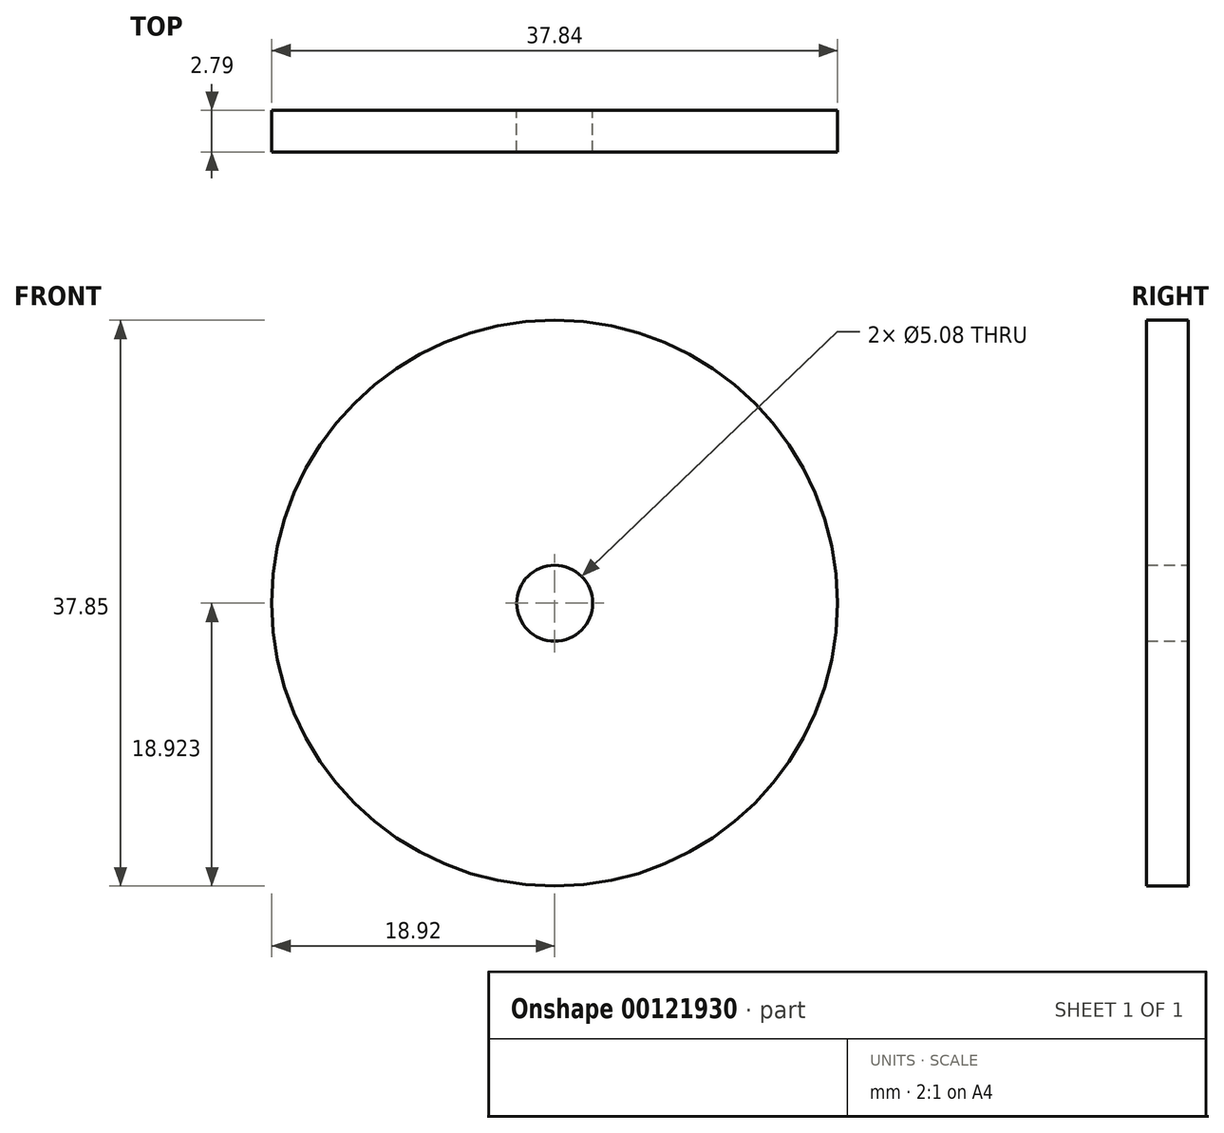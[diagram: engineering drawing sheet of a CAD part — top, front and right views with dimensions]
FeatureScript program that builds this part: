
annotation { "Feature Type Name" : "Feature", "Feature Type Description" : "" }
export const myFeature = defineFeature(function(context is Context, id is Id, definition is map)
    precondition{}
    {
        {
            var Q0;
            Q0=qCreatedBy(makeId("Front.planeOp"),FACE);
            var sketch = newSketch(context, id + "F0", { "sketchPlane" : qUnion([Q0])});
            skCircle(sketch, "E0", {"center": v(0, 2.17) * mm, "radius": 18.92 * mm});
            skCircle(sketch, "E1", {"center": v(0, 2.17) * mm, "radius": 2.54 * mm});
            skSolve(sketch);
        }
        {
            var Q0;
            Q0 = qSketchRegion(id + "F0", true);
            extrude(context, id + "F1", {"entities" : qUnion([Q0]), "depth" : 2.8 * mm});
        }
    });
